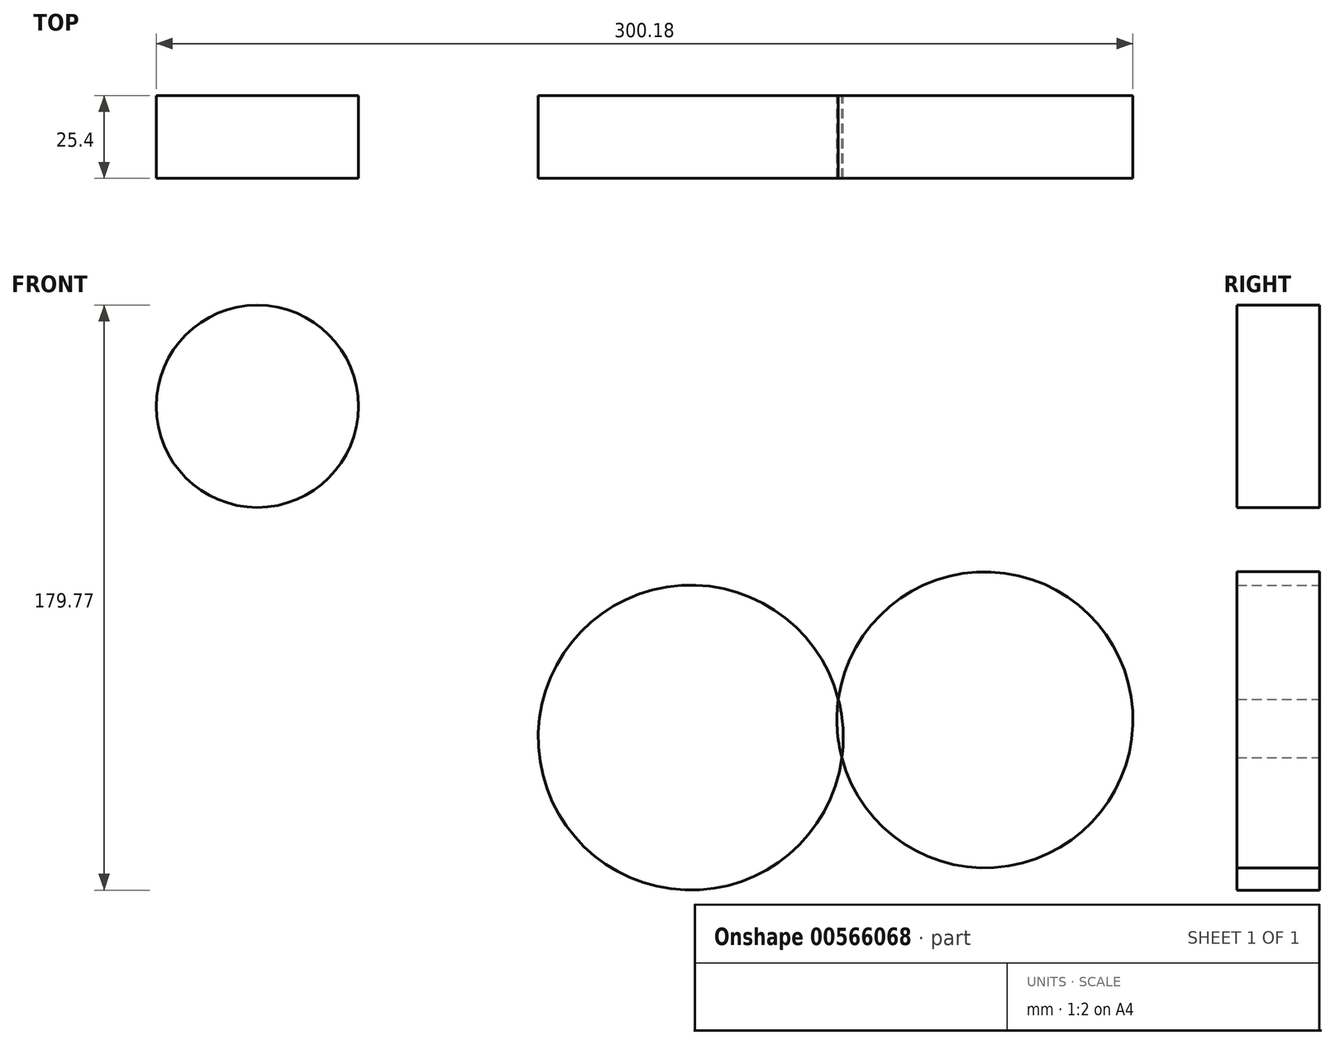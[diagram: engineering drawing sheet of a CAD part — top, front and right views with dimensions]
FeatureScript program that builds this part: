
annotation { "Feature Type Name" : "Feature", "Feature Type Description" : "" }
export const myFeature = defineFeature(function(context is Context, id is Id, definition is map)
    precondition{}
    {
        {
            var Q0;
            Q0=qCreatedBy(makeId("Front.planeOp"),FACE);
            var sketch = newSketch(context, id + "F0", { "sketchPlane" : qUnion([Q0])});
            skCircle(sketch, "E0", {"center": v(-45.37, -11.76) * mm, "radius": 46.87 * mm});
            skPoint(sketch, "E0.first.point", {"position": v(0, 0) * mm});
            skPoint(sketch, "E0.second.point", {"position": v(-90.74, 0) * mm});
            skPoint(sketch, "E0.third.point", {"position": v(0, -23.52) * mm});
            skCircle(sketch, "E1", {"center": v(45.05, -6.3) * mm, "radius": 45.48 * mm});
            skPoint(sketch, "E1.second.point", {"position": v(90.52, -7.12) * mm});
            skPoint(sketch, "E1.third.point", {"position": v(90.1, 0) * mm});
            skCircle(sketch, "E2", {"center": v(-178.57, 90.06) * mm, "radius": 31.08 * mm});
            skPoint(sketch, "E2.first.point", {"position": v(-202.42, 109.98) * mm});
            skPoint(sketch, "E2.second.point", {"position": v(-204.57, 73.04) * mm});
            skPoint(sketch, "E2.third.point", {"position": v(-150.34, 103.08) * mm});
            skSolve(sketch);
        }
        {
            var Q0;
            Q0 = qSketchRegion(id + "F0", true);
            var sketch = newSketch(context, id + "F1", { "sketchPlane" : qUnion([Q0])});
            skFitSpline(sketch, "E3", {"points": [v(-180.1, 88.68) * mm, v(51.54, 43.12) * mm, v(-57.88, 34.65) * mm, v(-196.2, 60.93) * mm, v(-180.1, 88.68) * mm]});
            skSolve(sketch);
        }
        {
            var Q0;
            Q0=makeQuery(id+"F0.imprint","IMPRINT",FACE,{"disambiguationData":[TD([[makeQuery(id+"F0.imprint","IMPRINT",EDGE,{"derivedFrom":sQuery(id+"F0.wireOp",EDGE,"E2")}),1.0]])]});
            var Q1;
            {var subQ0=sQuery(id+"F1.wireOp",EDGE,"E3");var subQ7=makeQuery(id+"F0.imprint","IMPRINT",EDGE,{"derivedFrom":sQuery(id+"F0.wireOp",EDGE,"E2")});var subQ9=makeQuery(id+"F1.imprint","INTERSECT",VERTEX,{"disambiguationData":[OD(0.0)],"derivedFrom":[subQ7,subQ0]});Q1=makeQuery(id+"F1.imprint","IMPRINT",FACE,{"disambiguationData":[TD([[makeQuery(id+"F1.imprint","IMPRINT",EDGE,{"disambiguationData":[TD([[subQ9,1.0]])],"derivedFrom":subQ7}),-1.0]])]});}
            var Q2;
            {var subQ0=sQuery(id+"F0.wireOp",EDGE,"E1");var subQ1=sQuery(id+"F0.wireOp",EDGE,"E0");var subQ2=makeQuery(id+"F0.imprint","INTERSECT",VERTEX,{"disambiguationData":[OD(0.0)],"derivedFrom":[subQ1,subQ0]});Q2=makeQuery(id+"F0.imprint","IMPRINT",FACE,{"disambiguationData":[TD([[makeQuery(id+"F0.imprint","IMPRINT",EDGE,{"disambiguationData":[TD([[subQ2,-1.0]])],"derivedFrom":subQ1}),-1.0]])]});}
            var Q3;
            {var subQ0=sQuery(id+"F0.wireOp",EDGE,"E1");var subQ1=sQuery(id+"F0.wireOp",EDGE,"E0");var subQ2=makeQuery(id+"F0.imprint","INTERSECT",VERTEX,{"disambiguationData":[OD(0.0)],"derivedFrom":[subQ1,subQ0]});Q3=makeQuery(id+"F0.imprint","IMPRINT",FACE,{"disambiguationData":[TD([[makeQuery(id+"F0.imprint","IMPRINT",EDGE,{"disambiguationData":[TD([[subQ2,1.0]])],"derivedFrom":subQ1}),1.0]])]});}
            extrude(context, id + "F2", {"entities" : qUnion([Q0, Q1, Q2, Q3]), "depth" : 25.4 * mm, "offsetDistance" : 25.4 * mm});
        }
    });
